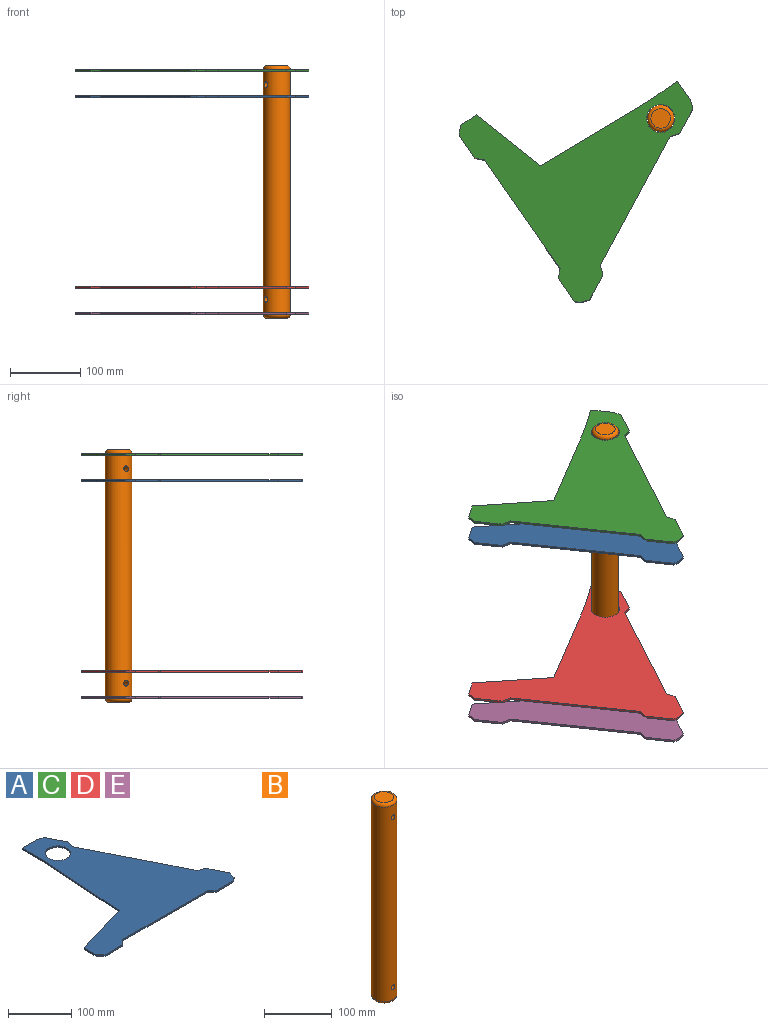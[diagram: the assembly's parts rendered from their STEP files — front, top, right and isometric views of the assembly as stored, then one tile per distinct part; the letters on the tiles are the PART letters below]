
ASSEMBLY  parts=5 mates=13
PART A: 22 faces, bbox 308.9x300x3 mm
  f0: plane 13.44x4.41mm, normal (0.31,0.95,0), area 42.4mm2, adj f1,f18,f20,f21
  f1: plane 31.81x3mm, normal (0,1,0), area 95.4mm2, adj f0,f2,f20,f21
  f2: plane 50x3mm, normal (-1,0,0), area 150mm2, adj f1,f3,f20,f21
  f3: plane 179.61x12.04mm, normal (-1,0.07,0), area 540mm2, adj f2,f4,f20,f21
  f4: plane 112.02x33.61mm, normal (-0.29,0.96,0), area 350.9mm2, adj f3,f5,f20,f21
  f5: plane 26.78x3mm, normal (-1,0,0), area 80.3mm2, adj f4,f6,f20,f21
  f6: plane 10x10mm, normal (-0.71,-0.71,0), area 42.4mm2, adj f5,f7,f20,f21
  f7: plane 40x3mm, normal (0,-1,0), area 120mm2, adj f6,f8,f20,f21
  f8: plane 10x10mm, normal (0.71,-0.71,0), area 42.4mm2, adj f7,f9,f20,f21
  f9: plane 188.68x3mm, normal (0,-1,0), area 566mm2, adj f8,f10,f20,f21
  f10: plane 10x10mm, normal (-0.71,-0.71,0), area 42.4mm2, adj f9,f11,f20,f21
  f11: plane 40x3mm, normal (0,-1,0), area 120mm2, adj f10,f12,f20,f21
  f12: plane 5.86x5.86mm, normal (0.71,-0.71,0), area 24.8mm2, adj f11,f13,f20,f21
  f13: plane 13.44x4.41mm, normal (0.95,-0.31,0), area 42.4mm2, adj f12,f14,f20,f21
  f14: plane 35.7x18.04mm, normal (0.89,0.45,0), area 120mm2, adj f13,f15,f20,f21
  f15: plane 13.44x4.41mm, normal (0.31,0.95,0), area 42.4mm2, adj f14,f16,f20,f21
  f16: plane 187.05x94.53mm, normal (0.89,0.45,0), area 628.7mm2, adj f15,f17,f20,f21
  f17: plane 13.44x4.41mm, normal (0.95,-0.31,0), area 42.4mm2, adj f16,f18,f20,f21
  f18: plane 35.7x18.04mm, normal (0.89,0.45,0), area 120mm2, adj f0,f17,f20,f21
  f19: cylinder r=20mm len=40mm, axis (0,0,-1), area 377mm2, adj f20,f21
  f20: plane 308.94x300mm, normal (0,0,1), area 37898.2mm2, adj f0,f1,f2,f3,f4,f5,f6,f7
  f21: plane 308.94x300mm, normal (0,0,-1), area 37898.2mm2, adj f0,f1,f2,f3,f4,f5,f6,f7
PART B: 7 faces, bbox 41.1x41.1x360 mm
  f0: cylinder r=19mm len=350mm, axis (0,0,-1), area 41580.1mm2, adj f3,f4,f5,f6
  f1: plane 28x28mm, normal (0,0,1), area 615.8mm2, adj f4
  f2: plane 28x28mm, normal (0,0,-1), area 615.8mm2, adj f3
  f3: torus R=14mm, axis (0,0,1), area 848mm2, adj f0,f2
  f4: torus R=14mm, axis (0,0,1), area 848mm2, adj f0,f1
  f5: cylinder r=4mm len=38mm, axis (0,1,0), area 944.4mm2, adj f0
  f6: cylinder r=4mm len=38mm, axis (0,1,0), area 944.4mm2, adj f0
PART C: same geometry as A
PART D: same geometry as A
PART E: same geometry as A
PLACE A rot(axis=(0,0,-1),55.3deg) t=(-134.51,52.31,476.27)mm
PLACE B rot(axis=(0,0,-1),55.3deg) t=(-134.51,52.31,161.66)mm
PLACE C rot(axis=(0,0,-1),55.3deg) t=(-134.51,52.31,513.27)mm
PLACE D rot(axis=(0,0,-1),55.3deg) t=(-134.51,52.31,204.14)mm
PLACE E rot(axis=(0,0,-1),55.3deg) t=(-134.51,52.31,167.14)mm
MATE cylindrical C.f19 <-> E.f19  axis (0,0,-1) through (-134.51,52.31,514.77)mm
MATE cylindrical C.f19 <-> A.f19  axis (0,0,-1) through (-134.51,52.31,513.27)mm
MATE parallel A.f21 <-> C.f20  axis (0,0,-1) through (-248.32,-42.93,476.27)mm
MATE parallel B.f0 <-> A.f21  axis (0,0,1) through (-134.51,52.31,166.66)mm
MATE planar D.f9 <-> E.f9  axis (-0.82,-0.57,0) through (-331.72,-84.46,205.64)mm
MATE parallel B.f0 <-> A.f21  axis (0,0,1) through (-134.51,52.31,166.66)mm
MATE cylindrical C.f19 <-> D.f19  axis (0,0,-1) through (-134.51,52.31,514.77)mm
MATE parallel B.f0 <-> D.f20  axis (0,0,1) through (-134.51,52.31,516.66)mm
MATE parallel B.f0 <-> D.f20  axis (0,0,1) through (-134.51,52.31,516.66)mm
MATE parallel E.f21 <-> D.f20  axis (0,0,-1) through (-248.32,-42.93,167.14)mm
MATE planar C.f9 <-> A.f9  axis (-0.82,-0.57,0) through (-331.72,-84.46,514.77)mm
MATE planar E.f9 <-> C.f9  axis (-0.82,-0.57,0) through (-331.72,-84.46,168.64)mm
MATE cylindrical A.f19 <-> B.f0  axis (0,0,-1) through (-134.51,52.31,477.77)mm
